# Revit family: equip-water-cooler-elkay-erpb
name_source: partatom
category: Plumbing Fixtures
units: mm (PartAtom-declared; Revit-internal decimal feet)

## family parameters
Always vertical = Yes
Cut with Voids When Loaded = No
OmniClass Number = 23.45.00.00
OmniClass Title = Sanitary, Laundry, and Cleaning Equipment
Part Type = Normal
Room Calculation Point = No
Round Connector Dimension = Use Radius
Shared = No
Work Plane-Based = No

## types (2) — shared parameters
Activation = Pushbutton
Basin Material = Metal - Steel - Stainless - Chrome
Bubbler = Flexi-Guard
CW Connection = Yes
Chiller = -
Cooler Depth = 1' - 7"
Cooler Width = 1' - 2"
Default Elevation = 0' - 0"
Description = Water Cooler
Filter = -
Fountian = -
HW Connection = No
Left Hand Unit = No
Lower Cooler Bottom = 1' - 0 3/8"
Lower Orifice Height = 2' - 9 15/16"
Manufacturer = Halsey Taylor
Model = ERPBM8K-HT
Mounting = -
Orifice to Rim = 0' - 1 5/8"
Panel Material = Metal - Steel - Stainless - Chrome
Right Hand Unit = Yes
Rim to CL Dispenser = 0' - 3 19/32"
Type = Single
URL = https://www.halseytaylor.com
Vent Connection = No
Version = 1.0.0.0
Volts/Hertz = 115V/60Hz
Waste Connection = Yes
Water Service Flow = 0 GPM
Water Service Size Radius = 0' - 0 1/4"

## type names (no varying parameters)
- ERPBM8K-HT
- LRPBM8K-HT

## geometry (parser evidence)
native form markers: Sweep x2
no freeform markers — native parametric forms only
